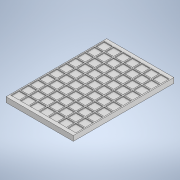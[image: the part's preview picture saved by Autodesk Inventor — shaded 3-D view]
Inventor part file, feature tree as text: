
AUTODESK INVENTOR PART (.ipt)
format: ipt  version: 2020 (Build 240168000, 168)  size: 288,768 bytes
history: native  units: in
note: dims shown in document units (in); Inventor stores cm internally (conversion verified against a paired STEP export)
features: extrude x2, sketch x2, pattern_linear x1
ambient origin geometry x8: Origin, YZ Plane, XZ Plane, XY Plane, X Axis, Y Axis, Z Axis, Center Point
bodies: Solid1 (feature_tree)
feature tree (5):
  extrude  "Extrusion1"  Depth=5.0299in
  extrude  "Extrusion2"  Depth=0.4724in
  pattern_linear  "Rectangular Pattern2"  Spacing1=0.25in  [1 undecoded]
  sketch  "Sketch1"  dims[d0=3.3654in d1=5.0299in]
  sketch  "Sketch3"  dims[d3=45.0deg d4=0.375in d5=0.25in d6=0.0in d23=0.0585in d24=0.1825in d25=0.4134in d26=0.4134in d27=0.0394in d28=0.0394in d29=0.0394in d30=0.0in d31=2.7559in d33=0.4724in d34=3.937in d36=0.4724in]
note: 1 required parameter value undecoded (feature->parameter linkage not recoverable at this tier; creation-order binding heuristic only, values carry confidence <= 0.55)
